# Revit family: IPDSC-DSE+
name_source: partatom
category: Communication Devices
revit_build: Autodesk Revit 2014 (Build: 20140709_2115(x64)
units: mm (PartAtom-declared; Revit-internal decimal feet)

## types (1)
- IP Dual Sided LED Display with Loudspeakers
    100V Taps = 32.00 W
    70V Taps = 32.00 W
    Baffle Material = <By Category>
    Body Material = Default
    Color = <By Category>
    Communication Ports = RJ-45 Female
    Cost = 1177.99 $
    Cost MSRP = 1177.99 $
    Coverage Horizontal = 110.00°
    Coverage Vertical = 110.00°
    Default Elevation = 48 "
    Depth = 7 "
    Description = POE+ IP COMPLIANT IP DUAL SIDED LED DISPLAY WITH FLASHER: INDOOR DUAL SIDED DISPLAY WITH LED FLASHER
    Enclosure Material = <By Category>
    Family Code (default) = LOUD SPEAKERS
    Grill Material = <By Category>
    Height = 4.21 "
    IQ Category = Audio Visual Intercoms
    Impedance = 8
    Ingress Protection = IP-XX (Not provided)
    Input Connectors = One Unbalanced Analog, Secured Screw Terminal Block, G.711, G.722 Capable
    Loudspeaker Level = 8Ω, 9W (802.3AF), 15W (802.3AT)
    Manufacturer = ATLAS SOUND
    Manufacturer URL = https://www.atlasied.com
    Market = Commercial, Higher Education, Emergency
    MasterFormat = 27 42 19
    MaterFormat Title = Public Information Systems
    Max Character Height = 2.125
    Model = IPDSC-DSE+
    Mount Material = Default
    Mounting/Rigging Provisions = Mounting Plate provided with Various Hole Patterns
    OmniClass Number = 23-37 27 15 13
    OmniClass Title = Audio Visual Intercoms
    Operation Mode = Self Powered
    Power Rating (RMS) = 15 Watts Max (802.3AT)
    Product Documentation Link = https://www.atlasied.com
    Product Page URL = https://www.atlasied.com
    Recommended Signal Processing = Built-In Processing
    SPL Max = 93
    Safety Agency Ratings = ETL Listed to Comply with UL-60950-1, and CAN/CSA-C22.2 No. 60950-1
    ScheduleType |RF| = AtlasIED Master
    Speaker Dispersion = 120.00°
    Speaker Type = S1
    Transformer Option = Yes
    URL = www.atlassound.com
    Vertical Symmetry = Yes
    Viewable Dimensions (HxW) = 10.125
    Voltage AC = PoE or PoE+ and External 24VDC
    Warranty = 1 Year
    Weight Product = 11
    Width = 9.91 "

## geometry (parser evidence)
native form markers: Blend x12, Sweep x8
no freeform markers — native parametric forms only
